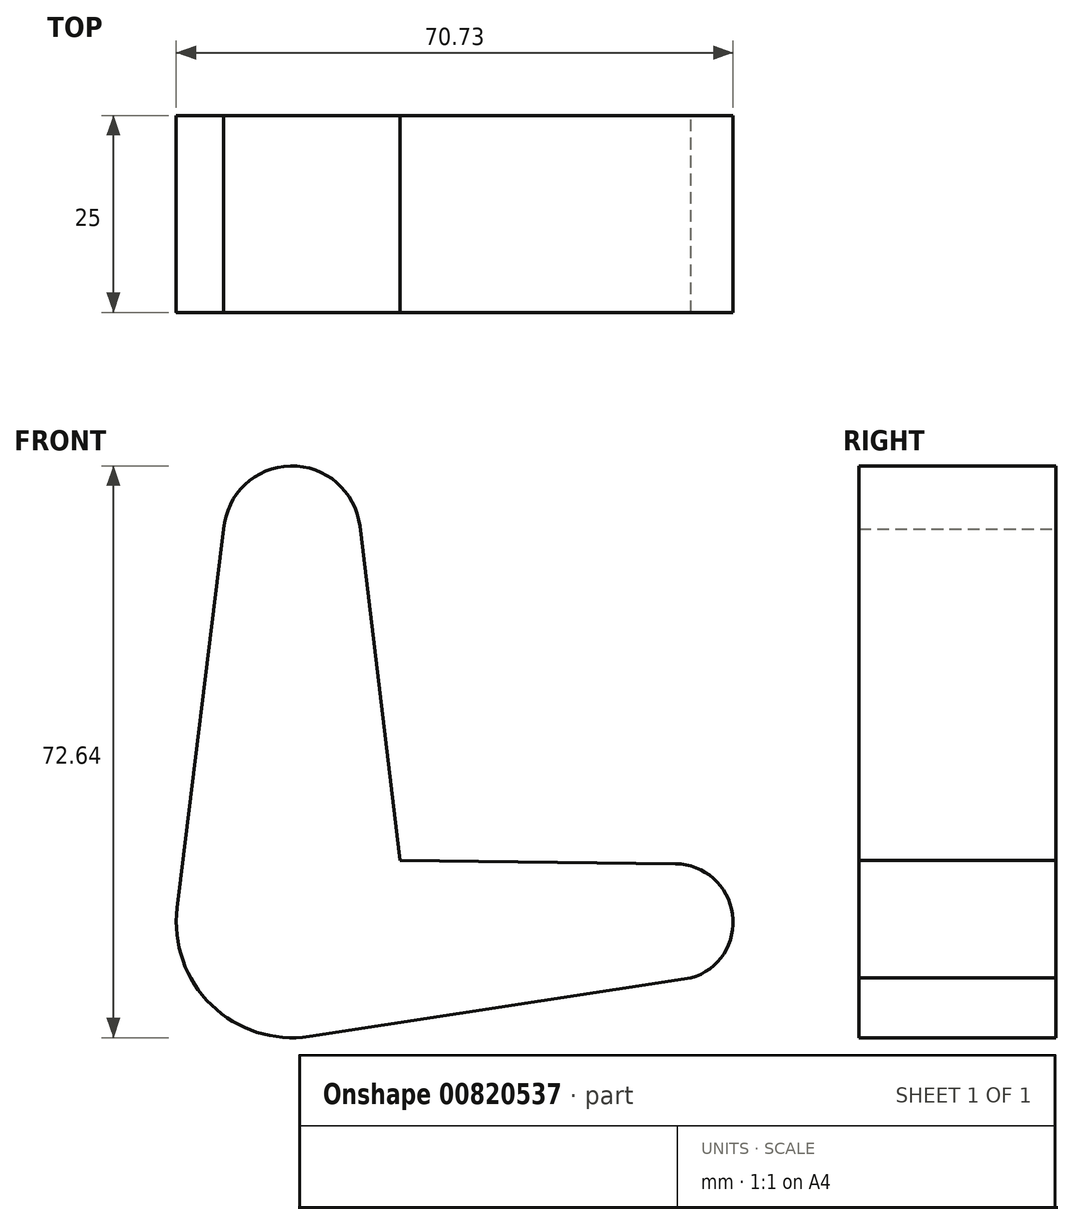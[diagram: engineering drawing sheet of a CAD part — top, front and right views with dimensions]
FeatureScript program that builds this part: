
annotation { "Feature Type Name" : "Feature", "Feature Type Description" : "" }
export const myFeature = defineFeature(function(context is Context, id is Id, definition is map)
    precondition{}
    {
        {
            var Q0;
            Q0=qCreatedBy(makeId("Front.planeOp"),FACE);
            var sketch = newSketch(context, id + "F0", { "sketchPlane" : qUnion([Q0])});
            skArc(sketch, "E0", {"start": v(8.63, 50.3) * mm, "mid": v(-0.2, 57.95) * mm, "end": v(-8.66, 49.9) * mm});
            skArc(sketch, "E1", {"start": v(-14.58, 1.8) * mm, "mid": v(-10.24, -10.54) * mm, "end": v(2.22, -14.53) * mm});
            skLineSegment(sketch, "E2", {"start": v(13.75, 7.86) * mm, "end": v(8.63, 50.3) * mm});
            skLineSegment(sketch, "E3", {"start": v(-8.66, 49.9) * mm, "end": v(-14.8, 0) * mm});
            skCircle(sketch, "E4", {"center": v(48.62, 0) * mm, "radius": 7.42 * mm});
            skLineSegment(sketch, "E5", {"start": v(50.7, -7.12) * mm, "end": v(0.86, -14.73) * mm});
            skPoint(sketch, "E5.endSnap0", {"position": v(0.86, -14.67) * mm});
            skLineSegment(sketch, "E6", {"start": v(48.72, 7.41) * mm, "end": v(13.75, 7.86) * mm});
            skPoint(sketch, "E7.orphan", {"position": v(14.7, 0) * mm});
            skSolve(sketch);
        }
        {
            var Q0;
            {var subQ1=sQuery(id+"F0.wireOp",EDGE,"E0");Q0=makeQuery(id+"F0.imprint","IMPRINT",FACE,{"disambiguationData":[TD([[makeQuery(id+"F0.imprint","IMPRINT",EDGE,{"derivedFrom":subQ1}),1.0]])]});}
            var Q1;
            {var subQ0=sQuery(id+"F0.wireOp",EDGE,"E4");var subQ1=makeQuery(id+"F0.imprint","INTERSECT",VERTEX,{"derivedFrom":[subQ0,sQuery(id+"F0.wireOp",EDGE,"E6")]});Q1=makeQuery(id+"F0.imprint","IMPRINT",FACE,{"disambiguationData":[TD([[makeQuery(id+"F0.imprint","IMPRINT",EDGE,{"disambiguationData":[TD([[subQ1,-1.0]])],"derivedFrom":subQ0}),1.0]])]});}
            extrude(context, id + "F1", {"entities" : qUnion([Q0, Q1]), "depth" : 25 * mm, "offsetDistance" : 25 * mm});
        }
    });
